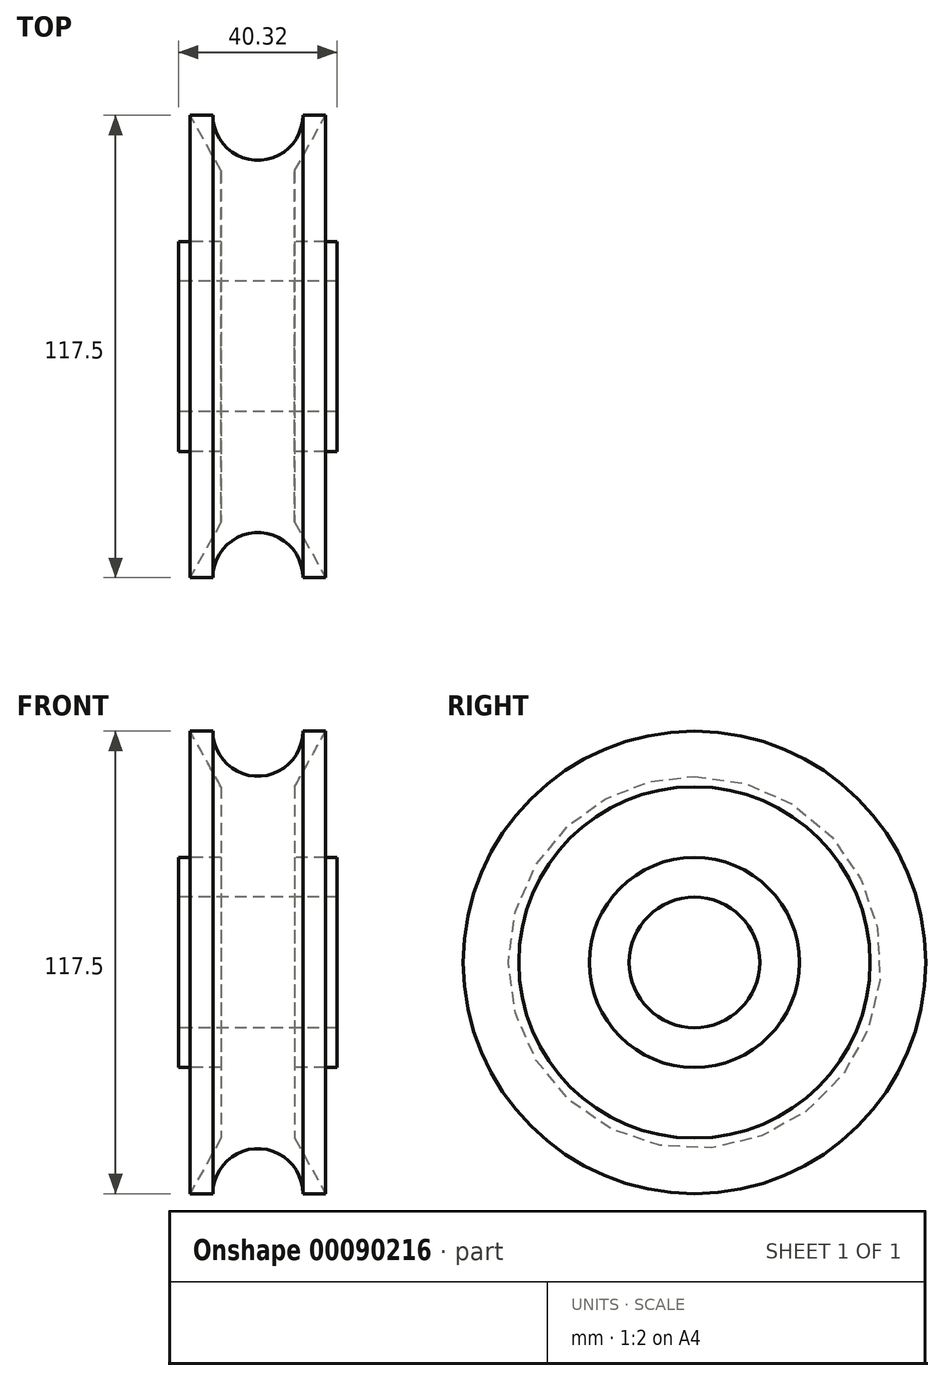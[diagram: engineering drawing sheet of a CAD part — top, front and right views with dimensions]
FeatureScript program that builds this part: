
annotation { "Feature Type Name" : "Feature", "Feature Type Description" : "" }
export const myFeature = defineFeature(function(context is Context, id is Id, definition is map)
    precondition{}
    {
        {
            var Q0;
            Q0=qCreatedBy(makeId("Front.planeOp"),FACE);
            var sketch = newSketch(context, id + "F0", { "sketchPlane" : qUnion([Q0])});
            skLineSegment(sketch, "E0", {"start": v(0, 45) * mm, "end": v(0, -35.65) * mm, "construction": true});
            skLineSegment(sketch, "E1", {"start": v(-44.72, 0) * mm, "end": v(33.54, 0) * mm, "construction": true});
            skLineSegment(sketch, "E2", {"start": v(0, 16.59) * mm, "end": v(-20.16, 16.59) * mm});
            skLineSegment(sketch, "E3", {"start": v(-20.16, 16.59) * mm, "end": v(-20.16, 26.67) * mm});
            skLineSegment(sketch, "E4", {"start": v(-20.16, 26.67) * mm, "end": v(-9.35, 26.67) * mm});
            skLineSegment(sketch, "E5", {"start": v(-9.35, 26.67) * mm, "end": v(-9.35, 44.63) * mm});
            skLineSegment(sketch, "E6", {"start": v(-9.35, 44.63) * mm, "end": v(-17.23, 58.75) * mm});
            skLineSegment(sketch, "E7", {"start": v(-17.23, 58.75) * mm, "end": v(-11.44, 58.75) * mm});
            skLineSegment(sketch, "E8.MirrorCS", {"start": v(17.23, 58.75) * mm, "end": v(11.44, 58.75) * mm});
            skLineSegment(sketch, "E9.MirrorCS", {"start": v(9.35, 44.63) * mm, "end": v(17.23, 58.75) * mm});
            skLineSegment(sketch, "E10.MirrorCS", {"start": v(9.35, 26.67) * mm, "end": v(9.35, 44.63) * mm});
            skLineSegment(sketch, "E11.MirrorCS", {"start": v(20.16, 26.67) * mm, "end": v(9.35, 26.67) * mm});
            skLineSegment(sketch, "E12.MirrorCS", {"start": v(20.16, 16.59) * mm, "end": v(20.16, 26.67) * mm});
            skLineSegment(sketch, "E13.MirrorCS", {"start": v(0, 16.59) * mm, "end": v(20.16, 16.59) * mm});
            skArc(sketch, "E14", {"start": v(-11.44, 58.75) * mm, "mid": v(0, 47.3) * mm, "end": v(11.44, 58.75) * mm});
            skSolve(sketch);
        }
        {
            var Q0;
            Q0 = qSketchRegion(id + "F0", true);
            var Q1;
            Q1=sQuery(id+"F0.wireOp",EDGE,"E1");
            revolve(context, id + "F1", {"entities" : qUnion([Q0]), "axis" : qUnion([Q1]), "revolveType" : RevolveType.FULL});
        }
    });
